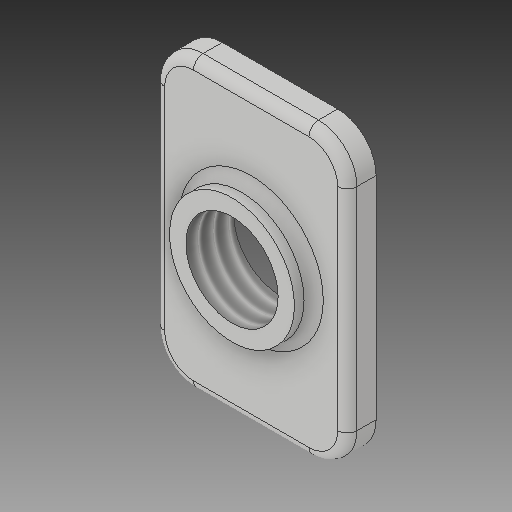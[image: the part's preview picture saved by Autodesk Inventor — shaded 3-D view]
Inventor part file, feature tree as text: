
AUTODESK INVENTOR PART (.ipt)
format: ipt  version: 2017 (Build 210142000, 142)  size: 174,592 bytes
history: native  units: mm
features: other x3, sketch x2
ambient origin geometry x8: Origin, YZ Plane, XZ Plane, XY Plane, X Axis, Y Axis, Z Axis, Center Point
bodies: Solid1 (feature_tree)
feature tree (5):
  other  "M5 Tee Nut-Generic_MIR_CPY.ipt"
  other  "Solid1::M5 Tee Nut-Generic_MIR_CPY.ipt"
  other  "TaggingFeature1"
  sketch  "Sketch1"  dims[d0=10.0mm]
  sketch  "Sketch2"
